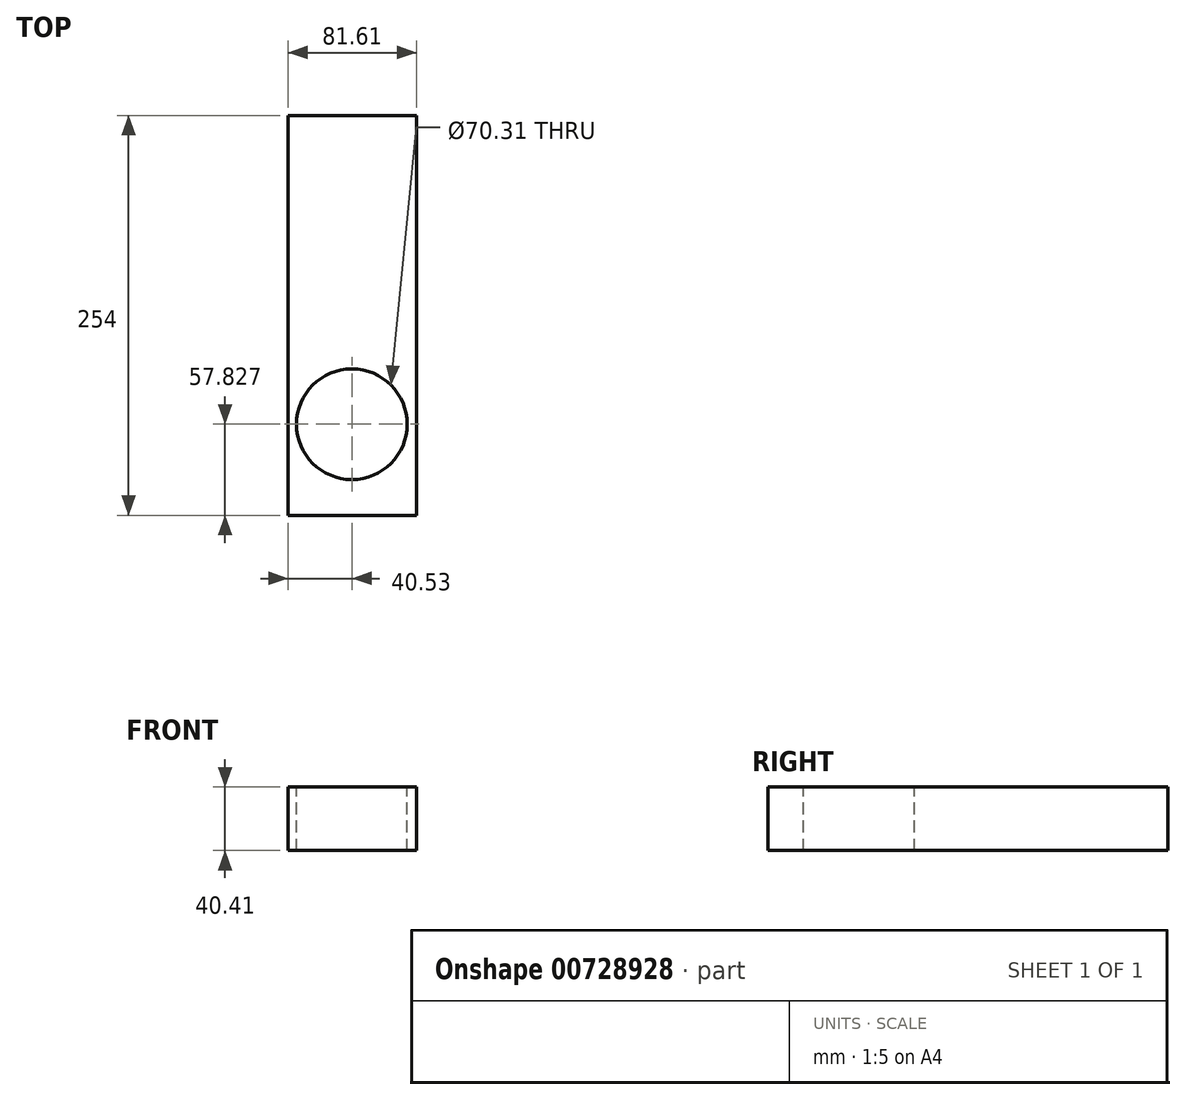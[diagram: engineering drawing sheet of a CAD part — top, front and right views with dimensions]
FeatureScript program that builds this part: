
annotation { "Feature Type Name" : "Feature", "Feature Type Description" : "" }
export const myFeature = defineFeature(function(context is Context, id is Id, definition is map)
    precondition{}
    {
        {
            var Q0;
            Q0=qCreatedBy(makeId("Front.planeOp"),FACE);
            var sketch = newSketch(context, id + "F0", { "sketchPlane" : qUnion([Q0])});
            skLineSegment(sketch, "E0.bottom", {"start": v(-27.78, 30.36) * mm, "end": v(53.83, 30.36) * mm});
            skLineSegment(sketch, "E0.top", {"start": v(-27.78, -10.05) * mm, "end": v(53.83, -10.05) * mm});
            skLineSegment(sketch, "E0.left", {"start": v(-27.78, 30.36) * mm, "end": v(-27.78, -10.05) * mm});
            skLineSegment(sketch, "E0.right", {"start": v(53.83, 30.36) * mm, "end": v(53.83, -10.05) * mm});
            skSolve(sketch);
        }
        {
            var Q0;
            Q0 = qSketchRegion(id + "F0", true);
            extrude(context, id + "F1", {"entities" : qUnion([Q0]), "depth" : 254 * mm, "offsetDistance" : 25.4 * mm});
        }
        {
            var Q0;
            Q0=makeQuery(id+"F1.opExtrude","SWEPT_FACE",FACE,{"disambiguationData":[OSD([sQuery(id+"F0.wireOp",EDGE,"E0.bottom")])]});
            var sketch = newSketch(context, id + "F2", { "sketchPlane" : qUnion([Q0])});
            skCircle(sketch, "E1", {"center": v(12.75, -196.17) * mm, "radius": 35.15 * mm});
            skSolve(sketch);
        }
        {
            var Q0;
            Q0=makeQuery(id+"F2.imprint","IMPRINT",FACE,{"disambiguationData":[TD([[makeQuery(id+"F2.imprint","IMPRINT",EDGE,{"derivedFrom":sQuery(id+"F2.wireOp",EDGE,"E1")}),1.0]])]});
            extrude(context, id + "F3", {"entities" : qUnion([Q0]), "operationType" : NewBodyOperationType.REMOVE, "oppositeDirection" : true, "depth" : 254 * mm, "offsetDistance" : 25.4 * mm});
        }
    });
